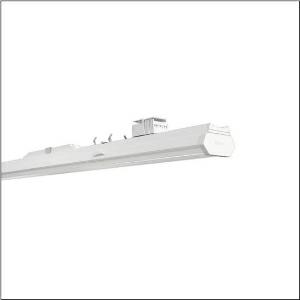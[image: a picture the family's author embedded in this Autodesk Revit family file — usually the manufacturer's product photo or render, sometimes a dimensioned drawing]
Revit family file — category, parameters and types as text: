
# Revit family: licross_r__11_protected_mo_51tp11cn48xf_8ef2
name_source: partatom
category: Lighting Fixtures
units: mm (PartAtom-declared; Revit-internal decimal feet)

## family parameters
Cut with Voids When Loaded = No
Host = Face
Light Source = No
Part Type = Normal
Room Calculation Point = No
Round Connector Dimension = Use Diameter
Shared = No

## types (1)
- --- (1 x LED, 8140 lm, 49 W, 4000K)
    Apparent Load = 49 VA
    CIE Flux Codes = 83 94 98 100 100
    Color Rendering = 80
    Color Temperature = 4000K
    Default Elevation = 1800 mm
    Description = Licross® 11 Protected MOluminaire insert, length: 1.500mm, width: 90mm, height: 101mm, LED rated luminous flux: 8.140lm, light colour: 840, control gear: ON/OFF Multilumen, CLOi, control gear: ECG Multilumen, with plug, 3-pole, with phase selection, mains connection: 220..240V, AC, 50/60Hz, halogen-free wiring, primary optical cover: cover, of PMMA, light emission: direct with ceiling illumination distribution, protection rating (complete): IP64, insulation class (complete): insulation class I (protective earthing), certification: CE, ENEC, VDE, protection symbol: D if used in an environment with conductive dust loads with corresponding accessories, permissible ambient temperature for indoor applications: -35..+40°C, reducing of maximum allowable ambient temperature of 5°C with ceiling mounting, corresponds to IFS (International Featured Standards) requirements for safety and quality in the food industry, packaging unit: 1 piece
    Height = 92 mm
    Lamp = 1 x LED
    Lamp Light Flux = 8140 lm
    Lamp Power = 49 W
    Lamp count = 1
    Length = 1500 mm
    Luminous efficacy = 166 lm/W
    Manufacturer = Siteco
    ModVariant = No
    Model = 51TP11CN48XF
    Mounting Place = Ceiling
    Mounting Type = Pendant
    Number of Poles = 1
    OnlyDefault = Yes
    Power Factor = 1
    Product Name = Licross® 11 Protected MO
    Product group = luminaire insert
    ProductGroupID = 902
    Protection Class = Protection class I
    Protection Degree = IP 64
    RLX_Detail_Level = 1
    RlxData = <blob elided: 21457 chars, md5=9b0da19d>
    Socket = socket
    Standby Power = 0 W
    System Light Flux = 8140 lm
    System Power = 49 W
    Type Comments = factory setting: luminous flux: 100 % | (A | C | E) | 111 mA
    Type Image = l_1256148.jpg
    URL = http://relux.com
    VarID = @adj_137677
    Voltage = 0 V
    Weight = 0.00 kg
    Width = 88 mm

## geometry (parser evidence)
native form markers: Blend x4, Sweep x10
no freeform markers — native parametric forms only
